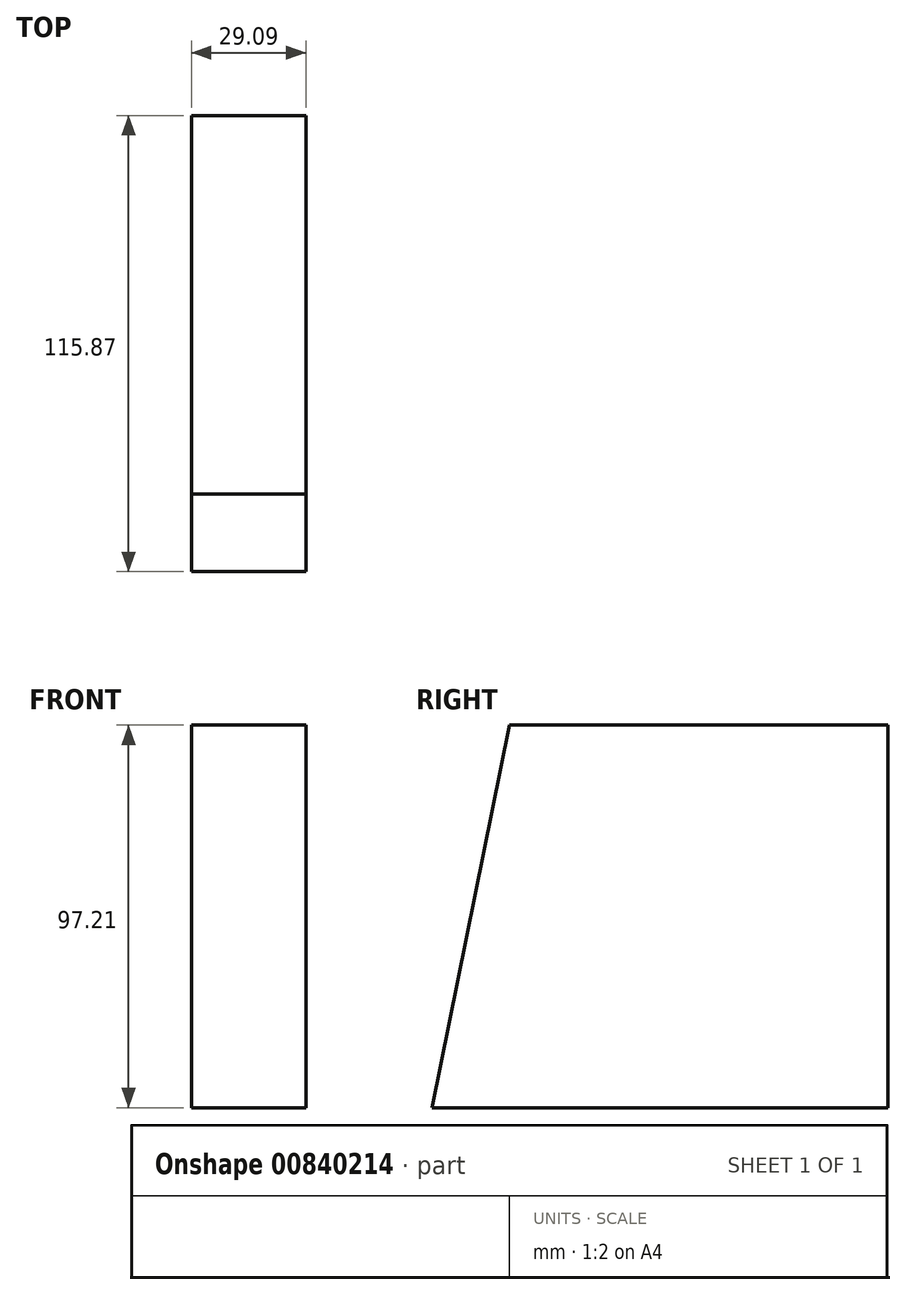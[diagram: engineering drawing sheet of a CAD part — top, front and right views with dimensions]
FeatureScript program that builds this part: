
annotation { "Feature Type Name" : "Feature", "Feature Type Description" : "" }
export const myFeature = defineFeature(function(context is Context, id is Id, definition is map)
    precondition{}
    {
        {
            var Q0;
            Q0=qCreatedBy(makeId("Right.planeOp"),FACE);
            var sketch = newSketch(context, id + "F0", { "sketchPlane" : qUnion([Q0])});
            skLineSegment(sketch, "E0", {"start": v(96.2, 0) * mm, "end": v(96.2, -97.2) * mm});
            skLineSegment(sketch, "E1", {"start": v(96.2, -97.2) * mm, "end": v(-19.68, -97.2) * mm});
            skLineSegment(sketch, "E2", {"start": v(-19.68, -97.2) * mm, "end": v(0, 0) * mm});
            skLineSegment(sketch, "E3", {"start": v(0, 0) * mm, "end": v(96.2, 0) * mm});
            skLineSegment(sketch, "E4", {"start": v(-130.23, 308.76) * mm, "end": v(0, 0) * mm});
            skSolve(sketch);
        }
        {
            var Q0;
            Q0 = qSketchRegion(id + "F0", true);
            extrude(context, id + "F1", {"entities" : qUnion([Q0]), "depth" : 29.09 * mm, "offsetDistance" : 25.4 * mm});
        }
    });
